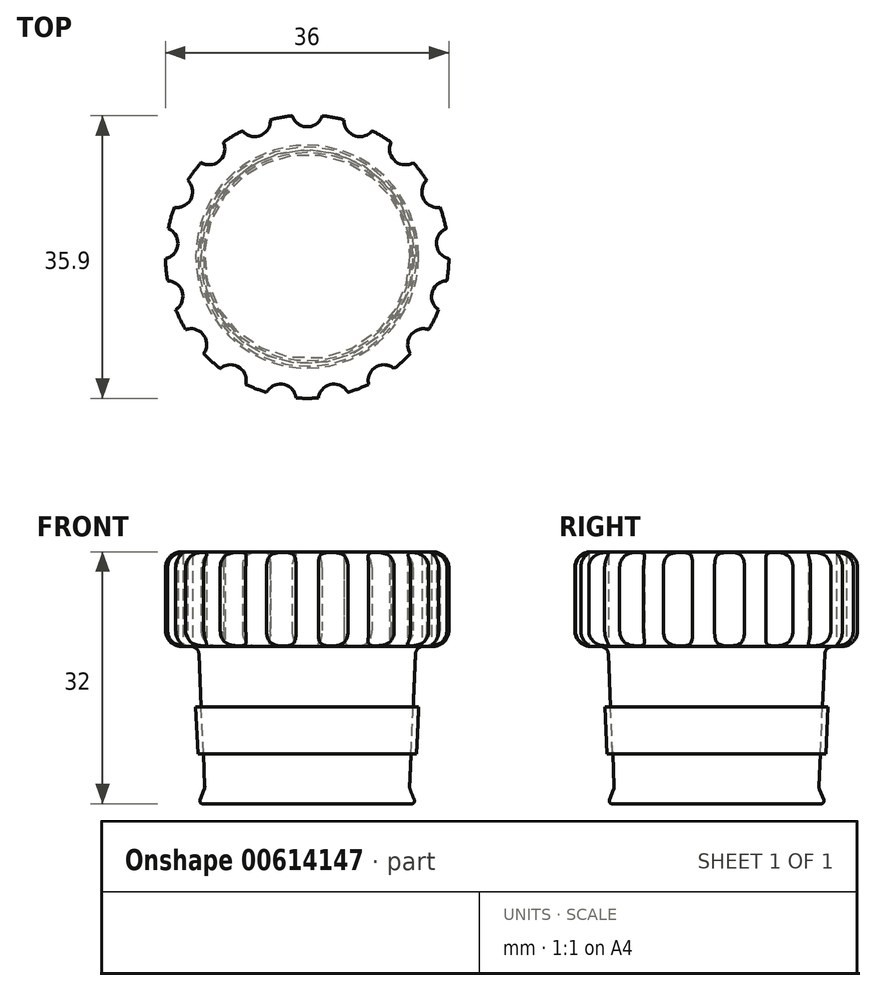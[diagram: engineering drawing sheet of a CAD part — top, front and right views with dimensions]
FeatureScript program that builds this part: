
annotation { "Feature Type Name" : "Feature", "Feature Type Description" : "" }
export const myFeature = defineFeature(function(context is Context, id is Id, definition is map)
    precondition{}
    {
        {
            var Q0;
            Q0=qCreatedBy(makeId("Front.planeOp"),FACE);
            var sketch = newSketch(context, id + "F0", { "sketchPlane" : qUnion([Q0])});
            skLineSegment(sketch, "E0", {"start": v(-13, -16.33) * mm, "end": v(-13.76, 0.5) * mm});
            skLineSegment(sketch, "E1", {"start": v(-14.76, 1.46) * mm, "end": v(-16, 1.46) * mm});
            skLineSegment(sketch, "E2", {"start": v(-18, 11.46) * mm, "end": v(-18, 3.46) * mm});
            skLineSegment(sketch, "E3", {"start": v(-16, 13.46) * mm, "end": v(0, 13.46) * mm});
            skPoint(sketch, "E4.visualSharp", {"position": v(-18, 13.46) * mm});
            skArc(sketch, "E4.filletArc", {"start": v(-16, 13.46) * mm, "mid": v(-17.41, 12.87) * mm, "end": v(-18, 11.46) * mm});
            skPoint(sketch, "E5.visualSharp", {"position": v(-13.8, 1.46) * mm});
            skArc(sketch, "E5.filletArc", {"start": v(-13.76, 0.5) * mm, "mid": v(-14.07, 1.18) * mm, "end": v(-14.76, 1.46) * mm});
            skPoint(sketch, "E6.visualSharp", {"position": v(-18, 1.46) * mm});
            skArc(sketch, "E6.filletArc", {"start": v(-18, 3.46) * mm, "mid": v(-17.41, 2.04) * mm, "end": v(-16, 1.46) * mm});
            skLineSegment(sketch, "E7", {"start": v(0, 13.46) * mm, "end": v(0, -18.54) * mm});
            skLineSegment(sketch, "E8", {"start": v(-13.08, -16.74) * mm, "end": v(-13.6, -18.06) * mm});
            skLineSegment(sketch, "E9", {"start": v(-13.28, -18.54) * mm, "end": v(0, -18.54) * mm});
            skPoint(sketch, "E10.visualSharp", {"position": v(-13, -16.54) * mm});
            skArc(sketch, "E10.filletArc", {"start": v(-13.08, -16.74) * mm, "mid": v(-13.02, -16.54) * mm, "end": v(-13, -16.33) * mm});
            skPoint(sketch, "E11.visualSharp", {"position": v(-13.8, -18.54) * mm});
            skArc(sketch, "E11.filletArc", {"start": v(-13.6, -18.06) * mm, "mid": v(-13.57, -18.39) * mm, "end": v(-13.28, -18.54) * mm});
            skSolve(sketch);
        }
        {
            var Q0;
            Q0=makeQuery(id+"F0.imprint","IMPRINT",FACE,{"disambiguationData":[TD([[makeQuery(id+"F0.imprint","IMPRINT",EDGE,{"derivedFrom":sQuery(id+"F0.wireOp",EDGE,"E0")}),-1.0]])]});
            var Q1;
            Q1=sQuery(id+"F0.wireOp",EDGE,"E7");
            revolve(context, id + "F1", {"entities" : qUnion([Q0]), "axis" : qUnion([Q1]), "revolveType" : RevolveType.FULL});
        }
        {
            var Q0;
            Q0=makeQuery(id+"F1.opRevolve","SWEPT_FACE",FACE,{"disambiguationData":[OSD([sQuery(id+"F0.wireOp",EDGE,"E3")])]});
            var sketch = newSketch(context, id + "F2", { "sketchPlane" : qUnion([Q0])});
            skCircle(sketch, "E12", {"center": v(0, 18.5) * mm, "radius": 2 * mm});
            skCircle(sketch, "E13.1.0", {"center": v(-6.68, 17.25) * mm, "radius": 2 * mm});
            skCircle(sketch, "E13.2.0", {"center": v(-12.46, 13.67) * mm, "radius": 2 * mm});
            skPoint(sketch, "E13.center", {"position": v(0, 0) * mm});
            skCircle(sketch, "E14.1.3.0", {"center": v(-16.56, 8.25) * mm, "radius": 2 * mm});
            skCircle(sketch, "E14.1.4.0", {"center": v(-18.42, 1.7) * mm, "radius": 2 * mm});
            skCircle(sketch, "E14.1.5.0", {"center": v(-17.8, -5.06) * mm, "radius": 2 * mm});
            skCircle(sketch, "E14.1.6.0", {"center": v(-14.76, -11.15) * mm, "radius": 2 * mm});
            skCircle(sketch, "E14.1.7.0", {"center": v(-9.74, -15.73) * mm, "radius": 2 * mm});
            skCircle(sketch, "E14.1.8.0", {"center": v(-3.4, -18.19) * mm, "radius": 2 * mm});
            skCircle(sketch, "E14.1.9.0", {"center": v(3.4, -18.19) * mm, "radius": 2 * mm});
            skCircle(sketch, "E14.1.10.0", {"center": v(9.74, -15.73) * mm, "radius": 2 * mm});
            skCircle(sketch, "E14.1.11.0", {"center": v(14.76, -11.15) * mm, "radius": 2 * mm});
            skCircle(sketch, "E14.1.12.0", {"center": v(17.8, -5.06) * mm, "radius": 2 * mm});
            skCircle(sketch, "E14.1.13.0", {"center": v(18.42, 1.7) * mm, "radius": 2 * mm});
            skCircle(sketch, "E14.1.14.0", {"center": v(16.56, 8.25) * mm, "radius": 2 * mm});
            skCircle(sketch, "E15.1.15.0", {"center": v(12.46, 13.67) * mm, "radius": 2 * mm});
            skCircle(sketch, "E15.1.16.0", {"center": v(6.68, 17.25) * mm, "radius": 2 * mm});
            skSolve(sketch);
        }
        {
            var Q0;
            Q0 = qSketchRegion(id + "F2", true);
            extrude(context, id + "F3", {"entities" : qUnion([Q0]), "operationType" : NewBodyOperationType.REMOVE, "depth" : 2 * mm, "offsetDistance" : 25 * mm, "hasSecondDirection" : true, "secondDirectionOppositeDirection" : true, "secondDirectionDepth" : 20 * mm});
        }
        {
            var Q0;
            Q0=qCreatedBy(makeId("Front.planeOp"),FACE);
            var sketch = newSketch(context, id + "F4", { "sketchPlane" : qUnion([Q0])});
            skLineSegment(sketch, "E16", {"start": v(-14.16, -6.24) * mm, "end": v(-13.9, -12.24) * mm});
            skLineSegment(sketch, "E17", {"start": v(-14.16, -6.24) * mm, "end": v(-13.46, -6.21) * mm});
            skLineSegment(sketch, "E18", {"start": v(-13.9, -12.24) * mm, "end": v(-13.2, -12.2) * mm});
            skLineSegment(sketch, "E19", {"start": v(-13.2, -12.2) * mm, "end": v(-13.46, -6.21) * mm});
            skSolve(sketch);
        }
        {
            var Q0;
            Q0=makeQuery(id+"F4.imprint","IMPRINT",FACE,{"disambiguationData":[TD([[makeQuery(id+"F4.imprint","IMPRINT",EDGE,{"derivedFrom":sQuery(id+"F4.wireOp",EDGE,"E16")}),1.0]])]});
            var Q1;
            Q1=sQuery(id+"F0.wireOp",EDGE,"E7");
            revolve(context, id + "F5", {"entities" : qUnion([Q0]), "axis" : qUnion([Q1]), "revolveType" : RevolveType.FULL});
        }
    });
